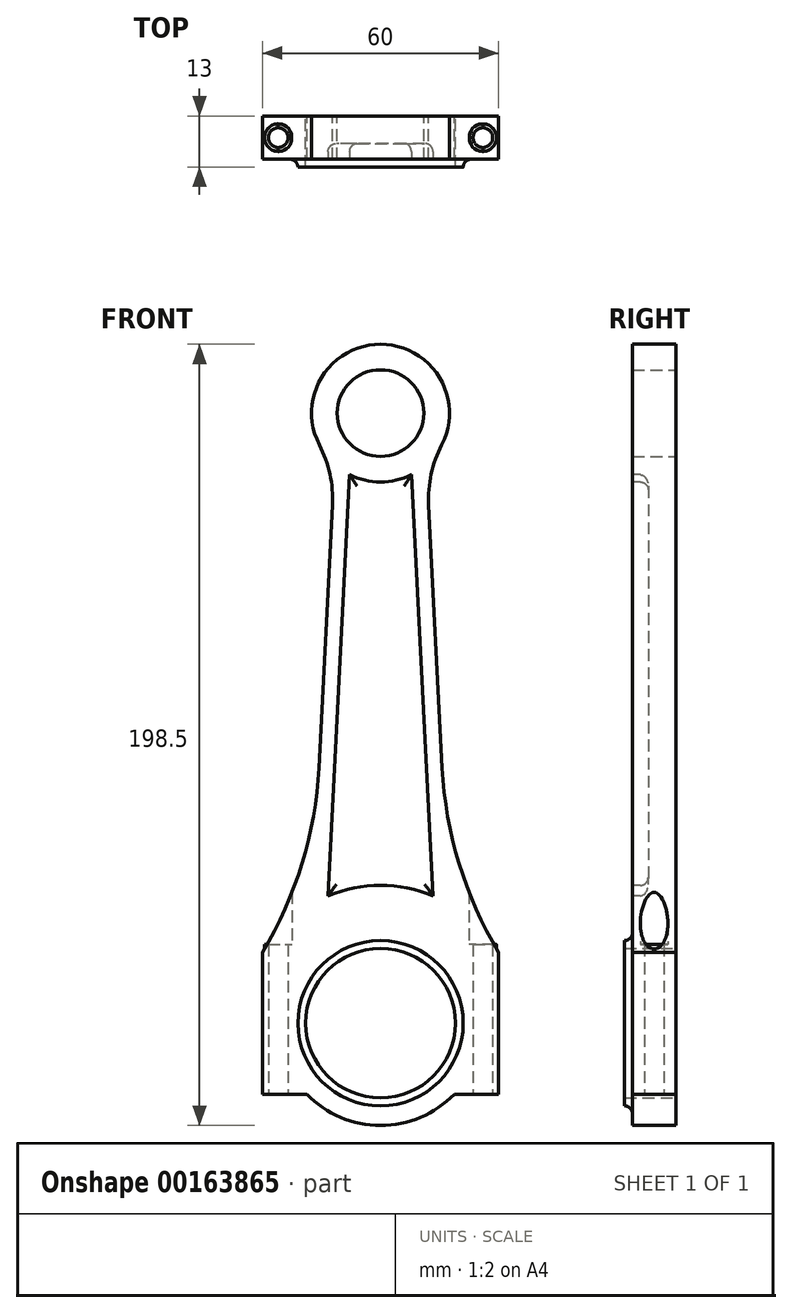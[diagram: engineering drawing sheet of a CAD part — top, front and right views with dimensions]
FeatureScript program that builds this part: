
annotation { "Feature Type Name" : "Feature", "Feature Type Description" : "" }
export const myFeature = defineFeature(function(context is Context, id is Id, definition is map)
    precondition{}
    {
        {
            var Q0;
            Q0=qCreatedBy(makeId("Front.planeOp"),FACE);
            var sketch = newSketch(context, id + "F0", { "sketchPlane" : qUnion([Q0])});
            skCircle(sketch, "E0", {"center": v(0, 0) * mm, "radius": 19 * mm});
            skCircle(sketch, "E1", {"center": v(0, 155) * mm, "radius": 11 * mm});
            skLineSegment(sketch, "E2", {"start": v(0, 155) * mm, "end": v(0, 0) * mm, "construction": true});
            skLineSegment(sketch, "E3", {"start": v(12.22, 131.62) * mm, "end": v(15.67, 64.9) * mm});
            skLineSegment(sketch, "E4.MirrorCS", {"start": v(-12.22, 131.62) * mm, "end": v(-15.67, 64.9) * mm});
            skArc(sketch, "E5", {"start": v(15.54, 146.96) * mm, "mid": v(0, 172.5) * mm, "end": v(-15.54, 146.96) * mm});
            skArc(sketch, "E6", {"start": v(30, 18.03) * mm, "mid": v(30, 18.04) * mm, "end": v(30, 18.04) * mm});
            skLineSegment(sketch, "E7", {"start": v(30, 18.03) * mm, "end": v(30, 0) * mm});
            skLineSegment(sketch, "E8.MirrorCS", {"start": v(-30, 18.03) * mm, "end": v(-30, 0) * mm});
            skLineSegment(sketch, "E9", {"start": v(0, 0) * mm, "end": v(102.28, 0) * mm, "construction": true});
            skLineSegment(sketch, "E10.MirrorCS", {"start": v(0, 0) * mm, "end": v(-102.28, 0) * mm, "construction": true});
            skLineSegment(sketch, "E11", {"start": v(-30, 18.03) * mm, "end": v(-30, 18.03) * mm});
            skPoint(sketch, "E12.newPointB", {"position": v(18.97, 0.98) * mm});
            skArc(sketch, "E12.filletArc", {"start": v(15.67, 64.9) * mm, "mid": v(19.95, 40.59) * mm, "end": v(30, 18.04) * mm});
            skPoint(sketch, "E13.newPointB", {"position": v(-18.97, 0.98) * mm});
            skArc(sketch, "E13.filletArc", {"start": v(-30, 18.03) * mm, "mid": v(-19.95, 40.58) * mm, "end": v(-15.67, 64.9) * mm});
            skPoint(sketch, "E14.orphan", {"position": v(-10.99, 155.57) * mm});
            skPoint(sketch, "E15.orphan", {"position": v(10.99, 155.57) * mm});
            skPoint(sketch, "E16.visualSharp", {"position": v(-11.69, 141.98) * mm});
            skArc(sketch, "E16.filletArc", {"start": v(-12.22, 131.62) * mm, "mid": v(-12.86, 139.5) * mm, "end": v(-15.54, 146.96) * mm});
            skPoint(sketch, "E17.visualSharp", {"position": v(11.69, 141.98) * mm});
            skArc(sketch, "E17.filletArc", {"start": v(15.54, 146.96) * mm, "mid": v(12.86, 139.5) * mm, "end": v(12.22, 131.62) * mm});
            skLineSegment(sketch, "E18", {"start": v(-30, 0) * mm, "end": v(-19, 0) * mm});
            skLineSegment(sketch, "E19", {"start": v(30, 0) * mm, "end": v(18.97, 0) * mm});
            skArc(sketch, "E20", {"start": v(-30, 18.03) * mm, "mid": v(0, -35) * mm, "end": v(30, 18.03) * mm});
            skLineSegment(sketch, "E21", {"start": v(-30, 0) * mm, "end": v(-30, -18.03) * mm});
            skLineSegment(sketch, "E22", {"start": v(30, 0) * mm, "end": v(30, -18.03) * mm});
            skCircle(sketch, "E23", {"center": v(0, 0) * mm, "radius": 26 * mm});
            skLineSegment(sketch, "E24", {"start": v(-30, -18.03) * mm, "end": v(-18.73, -18.03) * mm});
            skLineSegment(sketch, "E25", {"start": v(30, -18.03) * mm, "end": v(18.73, -18.03) * mm});
            skSolve(sketch);
        }
        {
            var Q0;
            Q0=makeQuery(id+"F0.imprint","IMPRINT",FACE,{"disambiguationData":[TD([[makeQuery(id+"F0.imprint","IMPRINT",EDGE,{"derivedFrom":sQuery(id+"F0.wireOp",EDGE,"E1")}),-1.0]])]});
            var Q1;
            {var subQ0=sQuery(id+"F0.wireOp",EDGE,"E18");var subQ1=sQuery(id+"F0.wireOp",EDGE,"E0");var subQ2=makeQuery(id+"F0.imprint","INTERSECT",VERTEX,{"derivedFrom":[subQ1,subQ0]});Q1=makeQuery(id+"F0.imprint","IMPRINT",FACE,{"disambiguationData":[TD([[makeQuery(id+"F0.imprint","IMPRINT",EDGE,{"disambiguationData":[TD([[subQ2,1.0]])],"derivedFrom":subQ1}),-1.0]])]});}
            extrude(context, id + "F1", {"entities" : qUnion([Q0, Q1]), "endBound" : BoundingType.SYMMETRIC, "depth" : 11 * mm});
        }
        {
            var Q0;
            Q0=makeQuery(id+"F1.opExtrude","CAP_FACE",FACE,{"disambiguationData":[OSD([sQuery(id+"F0.wireOp",EDGE,"E0"),sQuery(id+"F0.wireOp",EDGE,"E1"),sQuery(id+"F0.wireOp",EDGE,"E3"),sQuery(id+"F0.wireOp",EDGE,"E4.MirrorCS"),sQuery(id+"F0.wireOp",EDGE,"E5"),sQuery(id+"F0.wireOp",EDGE,"E6"),sQuery(id+"F0.wireOp",EDGE,"E7"),sQuery(id+"F0.wireOp",EDGE,"E8.MirrorCS"),sQuery(id+"F0.wireOp",EDGE,"E12.filletArc"),sQuery(id+"F0.wireOp",EDGE,"E13.filletArc"),sQuery(id+"F0.wireOp",EDGE,"E16.filletArc"),sQuery(id+"F0.wireOp",EDGE,"E17.filletArc"),sQuery(id+"F0.wireOp",EDGE,"E18"),sQuery(id+"F0.wireOp",EDGE,"E19")])],"isStart":false});
            var sketch = newSketch(context, id + "F2", { "sketchPlane" : qUnion([Q0])});
            skLineSegment(sketch, "E26", {"start": v(7.82, 139.34) * mm, "end": v(13.35, 32.35) * mm});
            skLineSegment(sketch, "E27", {"start": v(0, 155) * mm, "end": v(0, 0) * mm, "construction": true});
            skLineSegment(sketch, "E28.MirrorCS", {"start": v(-7.82, 139.34) * mm, "end": v(-13.35, 32.35) * mm});
            skArc(sketch, "E29", {"start": v(-7.82, 139.34) * mm, "mid": v(0, 137.5) * mm, "end": v(7.82, 139.34) * mm});
            skArc(sketch, "E30", {"start": v(13.35, 32.35) * mm, "mid": v(0, 35) * mm, "end": v(-13.35, 32.35) * mm});
            skSolve(sketch);
        }
        {
            var Q0;
            Q0=makeQuery(id+"F2.imprint","IMPRINT",FACE,{"disambiguationData":[TD([[makeQuery(id+"F2.imprint","IMPRINT",EDGE,{"derivedFrom":sQuery(id+"F2.wireOp",EDGE,"E26")}),-1.0]])]});
            extrude(context, id + "F3", {"entities" : qUnion([Q0]), "operationType" : NewBodyOperationType.REMOVE, "oppositeDirection" : true, "depth" : 4 * mm});
        }
        {
            var Q0;
            Q0=makeQuery(id+"F1.opExtrude","SWEPT_FACE",FACE,{"disambiguationData":[OSD([sQuery(id+"F0.wireOp",EDGE,"E18")])]});
            var sketch = newSketch(context, id + "F4", { "sketchPlane" : qUnion([Q0])});
            skCircle(sketch, "E31", {"center": v(-26, 0) * mm, "radius": 2.5 * mm});
            skCircle(sketch, "E32", {"center": v(26, 0) * mm, "radius": 2.5 * mm});
            skCircle(sketch, "E33.0", {"center": v(26, 0) * mm, "radius": 3.5 * mm});
            skCircle(sketch, "E34.0", {"center": v(-26, 0) * mm, "radius": 3.5 * mm});
            skSolve(sketch);
        }
        {
            var Q0;
            Q0=makeQuery(id+"F4.imprint","IMPRINT",FACE,{"disambiguationData":[TD([[makeQuery(id+"F4.imprint","IMPRINT",EDGE,{"derivedFrom":sQuery(id+"F4.wireOp",EDGE,"E31")}),-1.0]])]});
            var Q1;
            Q1=makeQuery(id+"F4.imprint","IMPRINT",FACE,{"disambiguationData":[TD([[makeQuery(id+"F4.imprint","IMPRINT",EDGE,{"derivedFrom":sQuery(id+"F4.wireOp",EDGE,"E31")}),1.0]])]});
            var Q2;
            Q2=makeQuery(id+"F4.imprint","IMPRINT",FACE,{"disambiguationData":[TD([[makeQuery(id+"F4.imprint","IMPRINT",EDGE,{"derivedFrom":sQuery(id+"F4.wireOp",EDGE,"E32")}),-1.0]])]});
            var Q3;
            Q3=makeQuery(id+"F4.imprint","IMPRINT",FACE,{"disambiguationData":[TD([[makeQuery(id+"F4.imprint","IMPRINT",EDGE,{"derivedFrom":sQuery(id+"F4.wireOp",EDGE,"E32")}),1.0]])]});
            extrude(context, id + "F5", {"entities" : qUnion([Q0, Q1, Q2, Q3]), "operationType" : NewBodyOperationType.REMOVE, "endBound" : BoundingType.UP_TO_NEXT, "oppositeDirection" : true, "depth" : 25.4 * mm});
        }
        {
            var Q0;
            Q0 = qSketchRegion(id + "F4", true);
            extrude(context, id + "F6", {"entities" : qUnion([Q0]), "operationType" : NewBodyOperationType.ADD, "oppositeDirection" : true, "depth" : 20 * mm});
        }
        {
            var Q0;
            Q0=makeQuery(id+"F1.opExtrude","CAP_FACE",FACE,{"disambiguationData":[OSD([sQuery(id+"F0.wireOp",EDGE,"E0"),sQuery(id+"F0.wireOp",EDGE,"E1"),sQuery(id+"F0.wireOp",EDGE,"E3"),sQuery(id+"F0.wireOp",EDGE,"E4.MirrorCS"),sQuery(id+"F0.wireOp",EDGE,"E5"),sQuery(id+"F0.wireOp",EDGE,"E6"),sQuery(id+"F0.wireOp",EDGE,"E7"),sQuery(id+"F0.wireOp",EDGE,"E8.MirrorCS"),sQuery(id+"F0.wireOp",EDGE,"E12.filletArc"),sQuery(id+"F0.wireOp",EDGE,"E13.filletArc"),sQuery(id+"F0.wireOp",EDGE,"E16.filletArc"),sQuery(id+"F0.wireOp",EDGE,"E17.filletArc"),sQuery(id+"F0.wireOp",EDGE,"E18"),sQuery(id+"F0.wireOp",EDGE,"E19")])],"isStart":false});
            var sketch = newSketch(context, id + "F7", { "sketchPlane" : qUnion([Q0])});
            skArc(sketch, "E35", {"start": v(21, 0) * mm, "mid": v(0, 21) * mm, "end": v(-21, 0) * mm});
            skArc(sketch, "E36.0", {"start": v(19, 0) * mm, "mid": v(0, 19) * mm, "end": v(-19, 0) * mm});
            skLineSegment(sketch, "E36.1", {"start": v(21, 0) * mm, "end": v(19, 0) * mm});
            skLineSegment(sketch, "E36.2", {"start": v(-21, 0) * mm, "end": v(-19, 0) * mm});
            skPoint(sketch, "E37.orphan", {"position": v(-30, 0) * mm});
            skPoint(sketch, "E38.orphan", {"position": v(30, 0) * mm});
            skSolve(sketch);
        }
        {
            var Q0;
            Q0=makeQuery(id+"F7.imprint","IMPRINT",FACE,{"disambiguationData":[TD([[makeQuery(id+"F7.imprint","IMPRINT",EDGE,{"derivedFrom":sQuery(id+"F7.wireOp",EDGE,"E35")}),1.0]])]});
            extrude(context, id + "F8", {"entities" : qUnion([Q0]), "operationType" : NewBodyOperationType.ADD, "depth" : 2 * mm});
        }
        {
            var Q0;
            Q0=makeQuery(id+"F8.opExtrude","CAP_EDGE",EDGE,{"disambiguationData":[OSD([sQuery(id+"F7.wireOp",EDGE,"E35")])],"isStart":true});
            var Q1;
            Q1=makeQuery(id+"F3.boolean.opBoolean","COPY",EDGE,{"derivedFrom":makeQuery(id+"F3.opExtrude","CAP_EDGE",EDGE,{"disambiguationData":[OSD([sQuery(id+"F2.wireOp",EDGE,"E30")])],"isStart":false})});
            var Q2;
            Q2=makeQuery(id+"F3.boolean.opBoolean","COPY",EDGE,{"derivedFrom":makeQuery(id+"F3.opExtrude","CAP_EDGE",EDGE,{"disambiguationData":[OSD([sQuery(id+"F2.wireOp",EDGE,"E28.MirrorCS")])],"isStart":false})});
            var Q3;
            Q3=makeQuery(id+"F3.boolean.opBoolean","COPY",EDGE,{"derivedFrom":makeQuery(id+"F3.opExtrude","CAP_EDGE",EDGE,{"disambiguationData":[OSD([sQuery(id+"F2.wireOp",EDGE,"E28.MirrorCS")])],"isStart":true})});
            var Q4;
            Q4=makeQuery(id+"F3.boolean.opBoolean","COPY",EDGE,{"derivedFrom":makeQuery(id+"F3.opExtrude","CAP_EDGE",EDGE,{"disambiguationData":[OSD([sQuery(id+"F2.wireOp",EDGE,"E30")])],"isStart":true})});
            var Q5;
            Q5=makeQuery(id+"F3.boolean.opBoolean","COPY",EDGE,{"derivedFrom":makeQuery(id+"F3.opExtrude","CAP_EDGE",EDGE,{"disambiguationData":[OSD([sQuery(id+"F2.wireOp",EDGE,"E26")])],"isStart":true})});
            var Q6;
            Q6=makeQuery(id+"F3.boolean.opBoolean","COPY",EDGE,{"derivedFrom":makeQuery(id+"F3.opExtrude","CAP_EDGE",EDGE,{"disambiguationData":[OSD([sQuery(id+"F2.wireOp",EDGE,"E26")])],"isStart":false})});
            var Q7;
            Q7=makeQuery(id+"F3.boolean.opBoolean","COPY",EDGE,{"derivedFrom":makeQuery(id+"F3.opExtrude","CAP_EDGE",EDGE,{"disambiguationData":[OSD([sQuery(id+"F2.wireOp",EDGE,"E29")])],"isStart":false})});
            var Q8;
            Q8=makeQuery(id+"F3.boolean.opBoolean","COPY",EDGE,{"derivedFrom":makeQuery(id+"F3.opExtrude","CAP_EDGE",EDGE,{"disambiguationData":[OSD([sQuery(id+"F2.wireOp",EDGE,"E29")])],"isStart":true})});
            var Q9;
            Q9=makeQuery(id+"FyyVKBtRcpZTXKV_1.1.F8.opExtrude","CAP_EDGE",EDGE,{"disambiguationData":[OSD([sQuery(id+"F7.wireOp",EDGE,"E35")])],"isStart":true});
            var Q10;
            Q10=makeQuery(id+"FfMMQ9owFz6AZpz_1.1.F3.boolean.opBoolean","COPY",EDGE,{"derivedFrom":makeQuery(id+"FfMMQ9owFz6AZpz_1.1.F3.opExtrude","CAP_EDGE",EDGE,{"disambiguationData":[OSD([sQuery(id+"F2.wireOp",EDGE,"E30")])],"isStart":false})});
            var Q11;
            Q11=makeQuery(id+"FfMMQ9owFz6AZpz_1.1.F3.boolean.opBoolean","COPY",EDGE,{"derivedFrom":makeQuery(id+"FfMMQ9owFz6AZpz_1.1.F3.opExtrude","CAP_EDGE",EDGE,{"disambiguationData":[OSD([sQuery(id+"F2.wireOp",EDGE,"E28.MirrorCS")])],"isStart":false})});
            var Q12;
            Q12=makeQuery(id+"FfMMQ9owFz6AZpz_1.1.F3.boolean.opBoolean","COPY",EDGE,{"derivedFrom":makeQuery(id+"FfMMQ9owFz6AZpz_1.1.F3.opExtrude","CAP_EDGE",EDGE,{"disambiguationData":[OSD([sQuery(id+"F2.wireOp",EDGE,"E28.MirrorCS")])],"isStart":true})});
            var Q13;
            Q13=makeQuery(id+"FfMMQ9owFz6AZpz_1.1.F3.boolean.opBoolean","COPY",EDGE,{"derivedFrom":makeQuery(id+"FfMMQ9owFz6AZpz_1.1.F3.opExtrude","CAP_EDGE",EDGE,{"disambiguationData":[OSD([sQuery(id+"F2.wireOp",EDGE,"E30")])],"isStart":true})});
            var Q14;
            Q14=makeQuery(id+"FfMMQ9owFz6AZpz_1.1.F3.boolean.opBoolean","COPY",EDGE,{"derivedFrom":makeQuery(id+"FfMMQ9owFz6AZpz_1.1.F3.opExtrude","CAP_EDGE",EDGE,{"disambiguationData":[OSD([sQuery(id+"F2.wireOp",EDGE,"E26")])],"isStart":false})});
            var Q15;
            Q15=makeQuery(id+"FfMMQ9owFz6AZpz_1.1.F3.boolean.opBoolean","COPY",EDGE,{"derivedFrom":makeQuery(id+"FfMMQ9owFz6AZpz_1.1.F3.opExtrude","CAP_EDGE",EDGE,{"disambiguationData":[OSD([sQuery(id+"F2.wireOp",EDGE,"E29")])],"isStart":false})});
            var Q16;
            Q16=makeQuery(id+"FfMMQ9owFz6AZpz_1.1.F3.boolean.opBoolean","COPY",EDGE,{"derivedFrom":makeQuery(id+"FfMMQ9owFz6AZpz_1.1.F3.opExtrude","CAP_EDGE",EDGE,{"disambiguationData":[OSD([sQuery(id+"F2.wireOp",EDGE,"E29")])],"isStart":true})});
            var Q17;
            Q17=makeQuery(id+"FfMMQ9owFz6AZpz_1.1.F3.boolean.opBoolean","COPY",EDGE,{"derivedFrom":makeQuery(id+"FfMMQ9owFz6AZpz_1.1.F3.opExtrude","CAP_EDGE",EDGE,{"disambiguationData":[OSD([sQuery(id+"F2.wireOp",EDGE,"E26")])],"isStart":true})});
            fillet(context, id + "F9", {"entities" : qUnion([Q0, Q1, Q2, Q3, Q4, Q5, Q6, Q7, Q8, Q9, Q10, Q11, Q12, Q13, Q14, Q15, Q16, Q17]), "radius" : 2 * mm, "tangentPropagation" : true, "allowEdgeOverflow" : false});
        }
        {
            var Q0;
            {var subQ0=sQuery(id+"F0.wireOp",EDGE,"E18");var subQ1=sQuery(id+"F0.wireOp",EDGE,"E0");var subQ2=makeQuery(id+"F0.imprint","INTERSECT",VERTEX,{"derivedFrom":[subQ1,subQ0]});Q0=makeQuery(id+"F0.imprint","IMPRINT",FACE,{"disambiguationData":[TD([[makeQuery(id+"F0.imprint","IMPRINT",EDGE,{"disambiguationData":[TD([[subQ2,-1.0]])],"derivedFrom":subQ1}),-1.0]])]});}
            var Q1;
            {var subQ0=sQuery(id+"F0.wireOp",EDGE,"E21");Q1=makeQuery(id+"F0.imprint","IMPRINT",FACE,{"disambiguationData":[TD([[makeQuery(id+"F0.imprint","IMPRINT",EDGE,{"derivedFrom":subQ0}),1.0]])]});}
            var Q2;
            {var subQ0=sQuery(id+"F0.wireOp",EDGE,"E22");Q2=makeQuery(id+"F0.imprint","IMPRINT",FACE,{"disambiguationData":[TD([[makeQuery(id+"F0.imprint","IMPRINT",EDGE,{"derivedFrom":subQ0}),-1.0]])]});}
            extrude(context, id + "F10", {"entities" : qUnion([Q0, Q1, Q2]), "endBound" : BoundingType.SYMMETRIC, "depth" : 11 * mm});
        }
        {
            var Q0;
            Q0=makeQuery(id+"F10.opExtrude","CAP_FACE",FACE,{"disambiguationData":[OSD([sQuery(id+"F0.wireOp",EDGE,"E0"),sQuery(id+"F0.wireOp",EDGE,"E18"),sQuery(id+"F0.wireOp",EDGE,"E19"),sQuery(id+"F0.wireOp",EDGE,"E21"),sQuery(id+"F0.wireOp",EDGE,"E22"),sQuery(id+"F0.wireOp",EDGE,"E23"),sQuery(id+"F0.wireOp",EDGE,"E24"),sQuery(id+"F0.wireOp",EDGE,"E25")])],"isStart":false});
            var sketch = newSketch(context, id + "F11", { "sketchPlane" : qUnion([Q0])});
            skCircle(sketch, "E39.0", {"center": v(0, 0) * mm, "radius": 19 * mm});
            skLineSegment(sketch, "E40", {"start": v(-19, 0) * mm, "end": v(-21, 0) * mm});
            skLineSegment(sketch, "E41", {"start": v(19, 0) * mm, "end": v(21, 0) * mm});
            skArc(sketch, "E42", {"start": v(-21, 0) * mm, "mid": v(0, -21) * mm, "end": v(21, 0) * mm});
            skSolve(sketch);
        }
        {
            var Q0;
            {var subQ0=sQuery(id+"F11.wireOp",EDGE,"E40");Q0=makeQuery(id+"F11.imprint","IMPRINT",FACE,{"disambiguationData":[TD([[makeQuery(id+"F11.imprint","IMPRINT",EDGE,{"derivedFrom":subQ0}),-1.0]])]});}
            extrude(context, id + "F12", {"entities" : qUnion([Q0]), "operationType" : NewBodyOperationType.ADD, "depth" : 2 * mm});
        }
        {
            var Q0;
            Q0=makeQuery(id+"F4.imprint","IMPRINT",FACE,{"disambiguationData":[TD([[makeQuery(id+"F4.imprint","IMPRINT",EDGE,{"derivedFrom":sQuery(id+"F4.wireOp",EDGE,"E32")}),1.0]])]});
            var Q1;
            Q1=makeQuery(id+"F4.imprint","IMPRINT",FACE,{"disambiguationData":[TD([[makeQuery(id+"F4.imprint","IMPRINT",EDGE,{"derivedFrom":sQuery(id+"F4.wireOp",EDGE,"E31")}),1.0]])]});
            extrude(context, id + "F13", {"entities" : qUnion([Q0, Q1]), "operationType" : NewBodyOperationType.REMOVE, "endBound" : BoundingType.UP_TO_NEXT, "depth" : 25.4 * mm});
        }
        {
            var Q0;
            Q0=makeQuery(id+"F12.opExtrude","CAP_EDGE",EDGE,{"disambiguationData":[OSD([sQuery(id+"F11.wireOp",EDGE,"E42")])],"isStart":true});
            fillet(context, id + "F14", {"entities" : qUnion([Q0]), "radius" : 2 * mm, "tangentPropagation" : true, "allowEdgeOverflow" : false});
        }
    });
